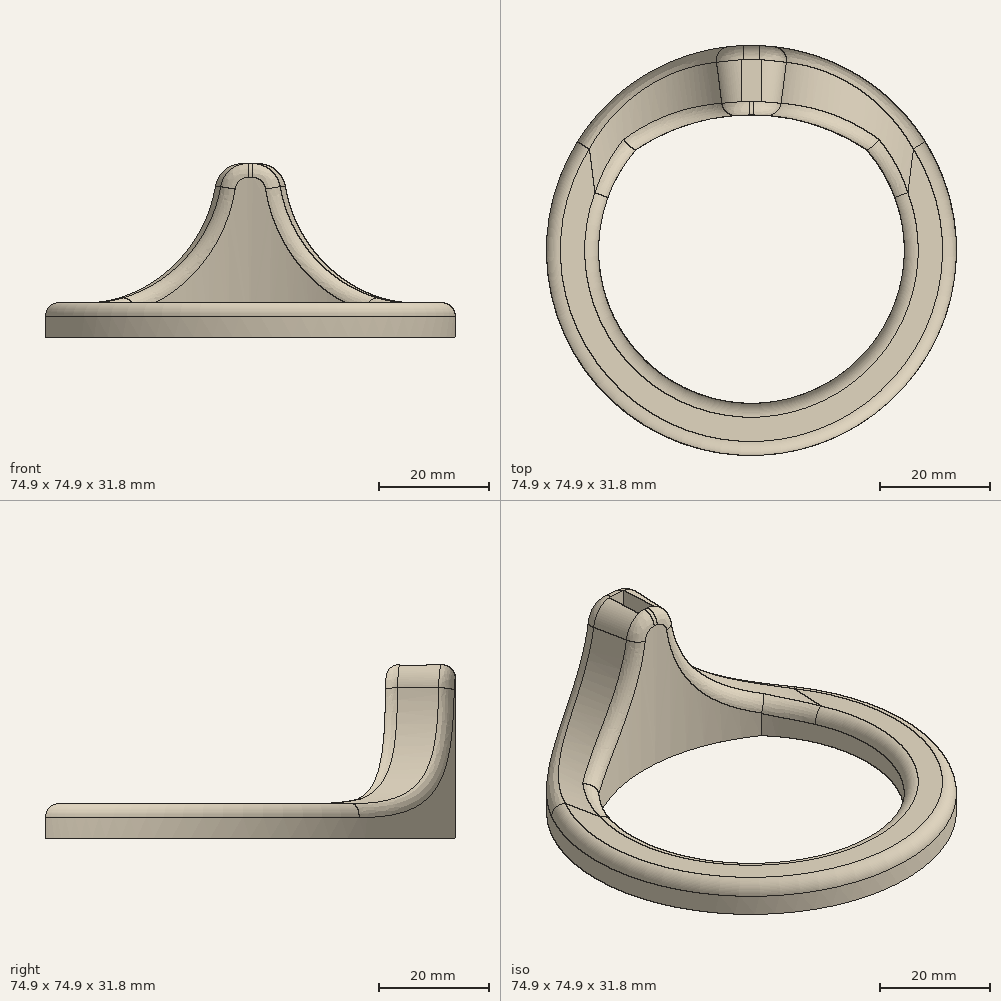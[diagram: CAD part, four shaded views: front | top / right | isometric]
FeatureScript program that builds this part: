
annotation { "Feature Type Name" : "Feature", "Feature Type Description" : "" }
export const myFeature = defineFeature(function(context is Context, id is Id, definition is map)
    precondition{}
    {
        {
            var Q0;
            Q0=qCreatedBy(makeId("Top.planeOp"),FACE);
            var sketch = newSketch(context, id + "F0", { "sketchPlane" : qUnion([Q0])});
            skCircle(sketch, "E0", {"center": v(0, 0) * mm, "radius": 37.47 * mm});
            skCircle(sketch, "E1", {"center": v(0, 0) * mm, "radius": 27.94 * mm});
            skArc(sketch, "E2", {"start": v(21.01, 18.42) * mm, "mid": v(0, 24.77) * mm, "end": v(-21.01, 18.42) * mm});
            skPoint(sketch, "E3", {"position": v(0, 37.47) * mm});
            skPoint(sketch, "E4", {"position": v(0, 24.77) * mm});
            skSolve(sketch);
        }
        {
            var Q0;
            Q0 = qSketchRegion(id + "F0", true);
            var Q1;
            {var subQ0=sQuery(id+"F0.wireOp",EDGE,"E2");Q1=makeQuery(id+"F0.imprint","IMPRINT",FACE,{"disambiguationData":[TD([[makeQuery(id+"F0.imprint","IMPRINT",EDGE,{"derivedFrom":subQ0}),-1.0]])]});}
            extrude(context, id + "F1", {"entities" : qUnion([Q0, Q1]), "depth" : 6.35 * mm});
        }
        {
            var Q0;
            Q0=makeQuery(id+"F1.opExtrude","CAP_FACE",FACE,{"disambiguationData":[OSD([sQuery(id+"F0.wireOp",EDGE,"E0"),sQuery(id+"F0.wireOp",EDGE,"E1"),sQuery(id+"F0.wireOp",EDGE,"E2")])],"isStart":false});
            var sketch = newSketch(context, id + "F2", { "sketchPlane" : qUnion([Q0])});
            skLineSegment(sketch, "E5.bottom", {"start": v(1.9, 34.93) * mm, "end": v(-1.9, 34.93) * mm});
            skLineSegment(sketch, "E5.top", {"start": v(1.9, 27.3) * mm, "end": v(-1.9, 27.3) * mm});
            skLineSegment(sketch, "E5.left", {"start": v(1.9, 34.93) * mm, "end": v(1.9, 27.3) * mm});
            skLineSegment(sketch, "E5.right", {"start": v(-1.9, 34.93) * mm, "end": v(-1.9, 27.3) * mm});
            skPoint(sketch, "E5.middle", {"position": v(0, 31.12) * mm});
            skLineSegment(sketch, "E6", {"start": v(0, 37.47) * mm, "end": v(0, 24.77) * mm, "construction": true});
            skArc(sketch, "E7", {"start": v(6.35, 36.92) * mm, "mid": v(0, 37.47) * mm, "end": v(-6.35, 36.92) * mm});
            skArc(sketch, "E8", {"start": v(4.76, 24.46) * mm, "mid": v(0, 24.77) * mm, "end": v(-4.76, 24.46) * mm});
            skLineSegment(sketch, "E9", {"start": v(4.76, 24.46) * mm, "end": v(6.35, 36.92) * mm});
            skLineSegment(sketch, "E10", {"start": v(-4.76, 24.46) * mm, "end": v(-6.35, 36.92) * mm});
            skSolve(sketch);
        }
        {
            var Q0;
            Q0 = qSketchRegion(id + "F2", true);
            extrude(context, id + "F3", {"entities" : qUnion([Q0]), "operationType" : NewBodyOperationType.ADD, "depth" : 25.4 * mm});
        }
        {
            var Q0;
            Q0=makeQuery(id+"F3.opExtrude","CAP_EDGE",EDGE,{"disambiguationData":[OSD([sQuery(id+"F2.wireOp",EDGE,"E9")])],"isStart":true});
            var Q1;
            Q1=makeQuery(id+"F3.opExtrude","CAP_EDGE",EDGE,{"disambiguationData":[OSD([sQuery(id+"F2.wireOp",EDGE,"E10")])],"isStart":true});
            fillet(context, id + "F4", {"entities" : qUnion([Q0, Q1]), "radius" : 25.4 * mm, "tangentPropagation" : true, "allowEdgeOverflow" : false});
        }
        {
            var Q0;
            {var subQ0=sQuery(id+"F2.wireOp",EDGE,"E9");Q0=makeQuery(id+"F4.opFillet","BLEND_EDGE",EDGE,{"blendedFrom":[makeQuery(id+"F3.opExtrude","CAP_EDGE",EDGE,{"disambiguationData":[OSD([subQ0])],"isStart":true}),makeQuery(id+"F3.opExtrude","CAP_FACE",FACE,{"disambiguationData":[OSD([sQuery(id+"F2.wireOp",EDGE,"E5.bottom"),sQuery(id+"F2.wireOp",EDGE,"E5.top"),sQuery(id+"F2.wireOp",EDGE,"E5.left"),sQuery(id+"F2.wireOp",EDGE,"E5.right"),sQuery(id+"F2.wireOp",EDGE,"E7"),sQuery(id+"F2.wireOp",EDGE,"E8"),subQ0,sQuery(id+"F2.wireOp",EDGE,"E10")])],"isStart":false})],"blendedInto":[makeQuery(id+"F3.opExtrude","CAP_FACE",FACE,{"disambiguationData":[OSD([sQuery(id+"F2.wireOp",EDGE,"E5.bottom"),sQuery(id+"F2.wireOp",EDGE,"E5.top"),sQuery(id+"F2.wireOp",EDGE,"E5.left"),sQuery(id+"F2.wireOp",EDGE,"E5.right"),sQuery(id+"F2.wireOp",EDGE,"E7"),sQuery(id+"F2.wireOp",EDGE,"E8"),subQ0,sQuery(id+"F2.wireOp",EDGE,"E10")])],"isStart":false})]});}
            var Q1;
            {var subQ0=sQuery(id+"F2.wireOp",EDGE,"E10");Q1=makeQuery(id+"F4.opFillet","BLEND_EDGE",EDGE,{"blendedFrom":[makeQuery(id+"F3.opExtrude","CAP_EDGE",EDGE,{"disambiguationData":[OSD([subQ0])],"isStart":true}),makeQuery(id+"F3.opExtrude","CAP_FACE",FACE,{"disambiguationData":[OSD([sQuery(id+"F2.wireOp",EDGE,"E5.bottom"),sQuery(id+"F2.wireOp",EDGE,"E5.top"),sQuery(id+"F2.wireOp",EDGE,"E5.left"),sQuery(id+"F2.wireOp",EDGE,"E5.right"),sQuery(id+"F2.wireOp",EDGE,"E7"),sQuery(id+"F2.wireOp",EDGE,"E8"),sQuery(id+"F2.wireOp",EDGE,"E9"),subQ0])],"isStart":false})],"blendedInto":[makeQuery(id+"F3.opExtrude","CAP_FACE",FACE,{"disambiguationData":[OSD([sQuery(id+"F2.wireOp",EDGE,"E5.bottom"),sQuery(id+"F2.wireOp",EDGE,"E5.top"),sQuery(id+"F2.wireOp",EDGE,"E5.left"),sQuery(id+"F2.wireOp",EDGE,"E5.right"),sQuery(id+"F2.wireOp",EDGE,"E7"),sQuery(id+"F2.wireOp",EDGE,"E8"),sQuery(id+"F2.wireOp",EDGE,"E9"),subQ0])],"isStart":false})]});}
            fillet(context, id + "F5", {"entities" : qUnion([Q0, Q1]), "radius" : 5.08 * mm, "tangentPropagation" : true, "allowEdgeOverflow" : false});
        }
        {
            var Q0;
            Q0=makeQuery(id+"F3.opExtrude","CAP_EDGE",EDGE,{"disambiguationData":[OSD([sQuery(id+"F2.wireOp",EDGE,"E8")])],"isStart":false});
            var Q1;
            Q1=makeQuery(id+"F3.opExtrude","CAP_EDGE",EDGE,{"disambiguationData":[OSD([sQuery(id+"F2.wireOp",EDGE,"E7")])],"isStart":false});
            var Q2;
            Q2=makeQuery(id+"F1.opExtrude","CAP_EDGE",EDGE,{"disambiguationData":[OSD([sQuery(id+"F0.wireOp",EDGE,"E1")])],"isStart":false});
            fillet(context, id + "F6", {"entities" : qUnion([Q0, Q1, Q2]), "radius" : 2.54 * mm, "tangentPropagation" : true, "allowEdgeOverflow" : false});
        }
    });
